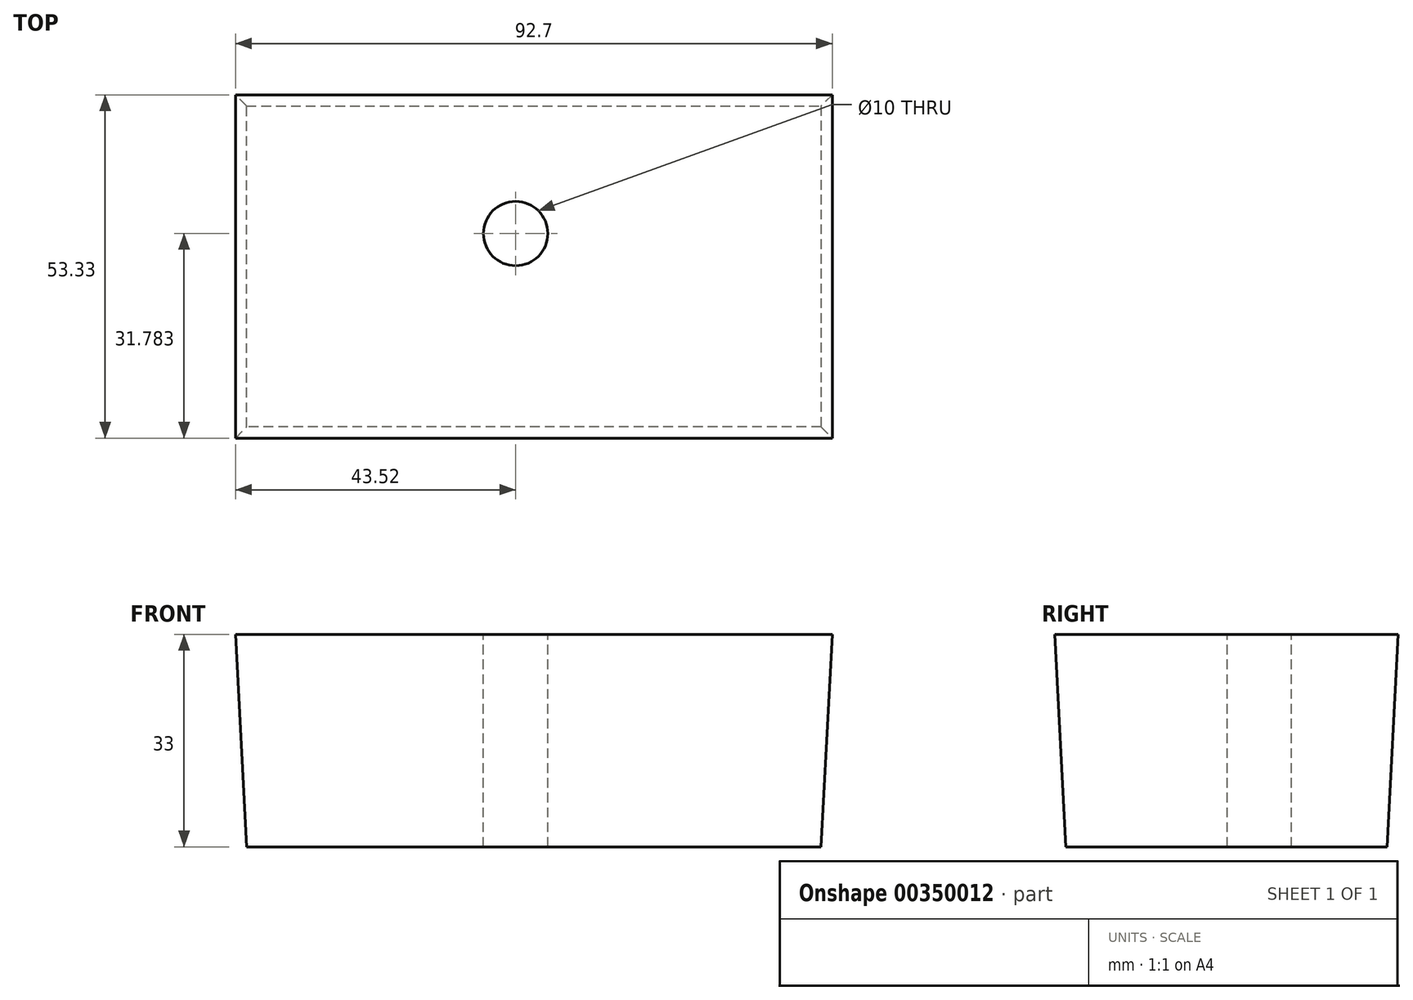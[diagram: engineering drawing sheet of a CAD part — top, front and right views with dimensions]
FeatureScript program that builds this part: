
annotation { "Feature Type Name" : "Feature", "Feature Type Description" : "" }
export const myFeature = defineFeature(function(context is Context, id is Id, definition is map)
    precondition{}
    {
        {
            var Q0;
            Q0=qCreatedBy(makeId("Top.planeOp"),FACE);
            var sketch = newSketch(context, id + "F0", { "sketchPlane" : qUnion([Q0])});
            skLineSegment(sketch, "E0.bottom", {"start": v(-41.8, 49.87) * mm, "end": v(47.45, 49.87) * mm});
            skLineSegment(sketch, "E0.top", {"start": v(-41.8, 0) * mm, "end": v(47.45, 0) * mm});
            skLineSegment(sketch, "E0.left", {"start": v(-41.8, 49.87) * mm, "end": v(-41.8, 0) * mm});
            skLineSegment(sketch, "E0.right", {"start": v(47.45, 49.87) * mm, "end": v(47.45, 0) * mm});
            skSolve(sketch);
        }
        {
            var Q0;
            Q0 = qSketchRegion(id + "F0", true);
            extrude(context, id + "F1", {"entities" : qUnion([Q0]), "depth" : 33 * mm, "hasDraft" : true, "draftAngle" : 3 * degree});
        }
        {
            var Q0;
            Q0=makeQuery(id+"F1.opExtrude","CAP_FACE",FACE,{"disambiguationData":[OSD([sQuery(id+"F0.wireOp",EDGE,"E0.bottom"),sQuery(id+"F0.wireOp",EDGE,"E0.top"),sQuery(id+"F0.wireOp",EDGE,"E0.left"),sQuery(id+"F0.wireOp",EDGE,"E0.right")])],"isStart":false});
            var sketch = newSketch(context, id + "F2", { "sketchPlane" : qUnion([Q0])});
            skSolve(sketch);
        }
        {
            var Q0;
            Q0=makeQuery(id+"F2.imprint","IMPRINT",FACE,{"disambiguationData":[TD([[makeQuery(id+"F2.imprint","IMPRINT",EDGE,{"derivedFrom":makeQuery(id+"F1.opExtrude","CAP_EDGE",EDGE,{"disambiguationData":[OSD([sQuery(id+"F0.wireOp",EDGE,"E0.bottom")])],"isStart":false})}),-1.0]])]});
            var sketch = newSketch(context, id + "F3", { "sketchPlane" : qUnion([Q0])});
            skSolve(sketch);
        }
        {
            var Q0;
            Q0=makeQuery(id+"F3.imprint","IMPRINT",FACE,{"disambiguationData":[TD([[makeQuery(id+"F3.imprint","IMPRINT",EDGE,{"derivedFrom":makeQuery(id+"F2.imprint","IMPRINT",EDGE,{"derivedFrom":makeQuery(id+"F1.opExtrude","CAP_EDGE",EDGE,{"disambiguationData":[OSD([sQuery(id+"F0.wireOp",EDGE,"E0.bottom")])],"isStart":false})})}),-1.0]])]});
            var sketch = newSketch(context, id + "F4", { "sketchPlane" : qUnion([Q0])});
            skLineSegment(sketch, "E1.bottom", {"start": v(0, 37.9) * mm, "end": v(0, 37.9) * mm});
            skLineSegment(sketch, "E1.top", {"start": v(0, 22.21) * mm, "end": v(0, 22.21) * mm});
            skLineSegment(sketch, "E1.left", {"start": v(0, 37.9) * mm, "end": v(0, 22.21) * mm});
            skLineSegment(sketch, "E1.right", {"start": v(0, 37.9) * mm, "end": v(0, 22.21) * mm});
            skPoint(sketch, "E1.middle", {"position": v(0, 30.05) * mm});
            skLineSegment(sketch, "E2.bottom", {"start": v(62.73, -24.16) * mm, "end": v(-23.66, -24.16) * mm});
            skLineSegment(sketch, "E2.top", {"start": v(62.73, 64.13) * mm, "end": v(-23.66, 64.13) * mm});
            skLineSegment(sketch, "E2.left", {"start": v(62.73, -24.16) * mm, "end": v(62.73, 64.13) * mm});
            skLineSegment(sketch, "E2.right", {"start": v(-23.66, -24.16) * mm, "end": v(-23.66, 64.13) * mm});
            skPoint(sketch, "E2.middle", {"position": v(19.54, 19.98) * mm});
            skSolve(sketch);
        }
        {
            var Q0;
            Q0=sQuery(id+"F4.wireOp",VERTEX,"E1.middle");
            var Q1;
            Q1=makeQuery(id+"F1.opExtrude","SWEPT_BODY",BODY,{"disambiguationData":[OSD([sQuery(id+"F0.wireOp",EDGE,"E0.bottom"),sQuery(id+"F0.wireOp",EDGE,"E0.top"),sQuery(id+"F0.wireOp",EDGE,"E0.left"),sQuery(id+"F0.wireOp",EDGE,"E0.right")])]});
            hole(context, id + "F5", {"style" : HoleStyle.SIMPLE, "endStyle" : HoleEndStyle.THROUGH, "holeDiameter" : 10 * mm, "isTappedThrough" : true, "tappedDepth" : 12 * mm, "tapClearance" : 3, "locations" : qUnion([Q0]), "scope" : qUnion([Q1])});
        }
    });
